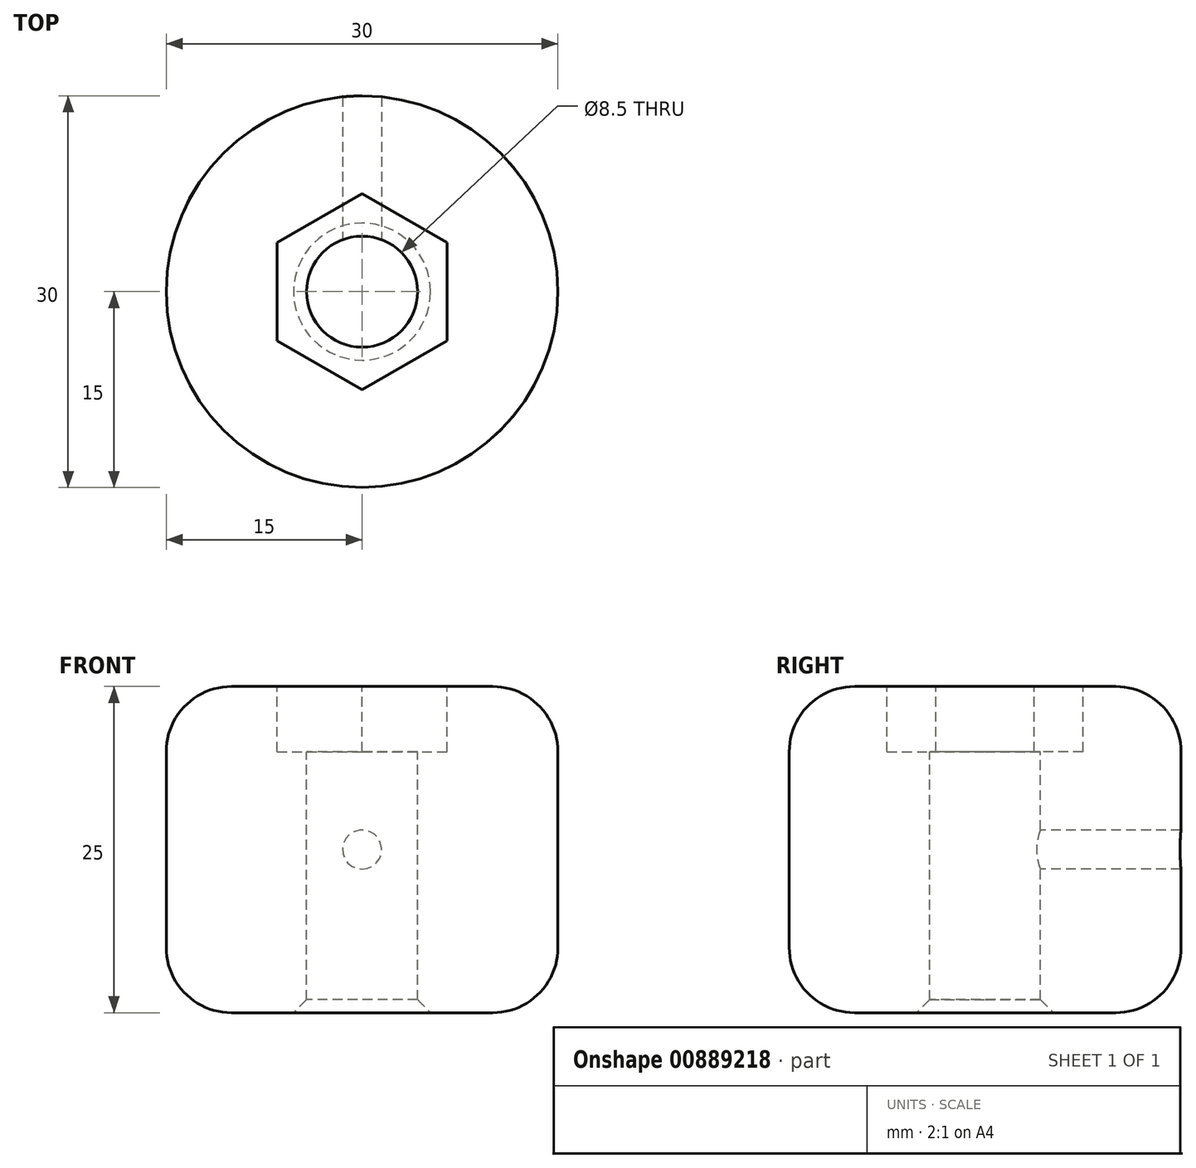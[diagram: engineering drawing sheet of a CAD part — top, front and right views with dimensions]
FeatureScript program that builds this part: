
annotation { "Feature Type Name" : "Feature", "Feature Type Description" : "" }
export const myFeature = defineFeature(function(context is Context, id is Id, definition is map)
    precondition{}
    {
        {
            var Q0;
            Q0=qCreatedBy(makeId("Top.planeOp"),FACE);
            var sketch = newSketch(context, id + "F0", { "sketchPlane" : qUnion([Q0])});
            skCircle(sketch, "E0", {"center": v(0, 0) * mm, "radius": 15 * mm});
            skSolve(sketch);
        }
        {
            var Q0;
            Q0=makeQuery(id+"F0.imprint","IMPRINT",FACE,{"disambiguationData":[TD([[makeQuery(id+"F0.imprint","IMPRINT",EDGE,{"derivedFrom":sQuery(id+"F0.wireOp",EDGE,"E0")}),1.0]])]});
            extrude(context, id + "F1", {"entities" : qUnion([Q0]), "endBound" : BoundingType.SYMMETRIC, "depth" : 25 * mm, "offsetDistance" : 25 * mm});
        }
        {
            var Q0;
            Q0=makeQuery(id+"F1.opExtrude","CAP_FACE",FACE,{"disambiguationData":[OSD([sQuery(id+"F0.wireOp",EDGE,"E0")])],"isStart":false});
            var sketch = newSketch(context, id + "F2", { "sketchPlane" : qUnion([Q0])});
            skCircle(sketch, "E1.cCircle", {"center": v(0, 0) * mm, "radius": 6.5 * mm, "construction": true});
            skLineSegment(sketch, "E1.0", {"start": v(6.5, 3.75) * mm, "end": v(6.5, -3.75) * mm});
            skLineSegment(sketch, "E1.1", {"start": v(6.5, -3.75) * mm, "end": v(0, -7.5) * mm});
            skLineSegment(sketch, "E1.2", {"start": v(0, -7.5) * mm, "end": v(-6.5, -3.75) * mm});
            skLineSegment(sketch, "E1.3", {"start": v(-6.5, -3.75) * mm, "end": v(-6.5, 3.75) * mm});
            skLineSegment(sketch, "E1.4", {"start": v(-6.5, 3.75) * mm, "end": v(0, 7.5) * mm});
            skLineSegment(sketch, "E1.5", {"start": v(0, 7.5) * mm, "end": v(6.5, 3.75) * mm});
            skPoint(sketch, "E1.0.midPoint", {"position": v(6.5, 0) * mm});
            skSolve(sketch);
        }
        {
            var Q0;
            Q0 = qSketchRegion(id + "F2", true);
            extrude(context, id + "F3", {"entities" : qUnion([Q0]), "operationType" : NewBodyOperationType.REMOVE, "oppositeDirection" : true, "depth" : 5 * mm, "offsetDistance" : 25 * mm});
        }
        {
            var Q0;
            Q0=makeQuery(id+"F3.boolean.opBoolean","COPY",FACE,{"derivedFrom":makeQuery(id+"F3.opExtrude","CAP_FACE",FACE,{"disambiguationData":[OSD([sQuery(id+"F2.wireOp",EDGE,"E1.0"),sQuery(id+"F2.wireOp",EDGE,"E1.1"),sQuery(id+"F2.wireOp",EDGE,"E1.2"),sQuery(id+"F2.wireOp",EDGE,"E1.3"),sQuery(id+"F2.wireOp",EDGE,"E1.4"),sQuery(id+"F2.wireOp",EDGE,"E1.5")])],"isStart":false})});
            var sketch = newSketch(context, id + "F4", { "sketchPlane" : qUnion([Q0])});
            skCircle(sketch, "E2", {"center": v(0, 0) * mm, "radius": 4.25 * mm});
            skSolve(sketch);
        }
        {
            var Q0;
            Q0 = qSketchRegion(id + "F4", true);
            extrude(context, id + "F5", {"entities" : qUnion([Q0]), "operationType" : NewBodyOperationType.REMOVE, "endBound" : BoundingType.THROUGH_ALL, "oppositeDirection" : true, "depth" : 25 * mm, "offsetDistance" : 25 * mm});
        }
        {
            var Q0;
            Q0=makeQuery(id+"F1.opExtrude","CAP_EDGE",EDGE,{"disambiguationData":[OSD([sQuery(id+"F0.wireOp",EDGE,"E0")])],"isStart":false});
            var Q1;
            Q1=makeQuery(id+"F1.opExtrude","CAP_EDGE",EDGE,{"disambiguationData":[OSD([sQuery(id+"F0.wireOp",EDGE,"E0")])],"isStart":true});
            fillet(context, id + "F6", {"entities" : qUnion([Q0, Q1]), "radius" : 5 * mm, "tangentPropagation" : true, "allowEdgeOverflow" : false});
        }
        {
            var Q0;
            Q0=makeQuery(id+"F5.boolean.opBoolean","INTERSECT",EDGE,{"derivedFrom":[makeQuery(id+"F1.opExtrude","CAP_FACE",FACE,{"disambiguationData":[OSD([sQuery(id+"F0.wireOp",EDGE,"E0")])],"isStart":true}),makeQuery(id+"F5.opExtrude","SWEPT_FACE",FACE,{"disambiguationData":[OSD([sQuery(id+"F4.wireOp",EDGE,"E2")])]})]});
            chamfer(context, id + "F7", {"entities" : qUnion([Q0]), "width" : 1 * mm, "tangentPropagation" : true});
        }
        {
            var Q0;
            Q0=qCreatedBy(makeId("Front.planeOp"),FACE);
            var sketch = newSketch(context, id + "F8", { "sketchPlane" : qUnion([Q0])});
            skCircle(sketch, "E3", {"center": v(0, 0) * mm, "radius": 1.5 * mm});
            skSolve(sketch);
        }
        {
            var Q0;
            Q0 = qSketchRegion(id + "F8", true);
            extrude(context, id + "F9", {"entities" : qUnion([Q0]), "operationType" : NewBodyOperationType.REMOVE, "oppositeDirection" : true, "depth" : 50 * mm, "offsetDistance" : 25 * mm});
        }
    });
